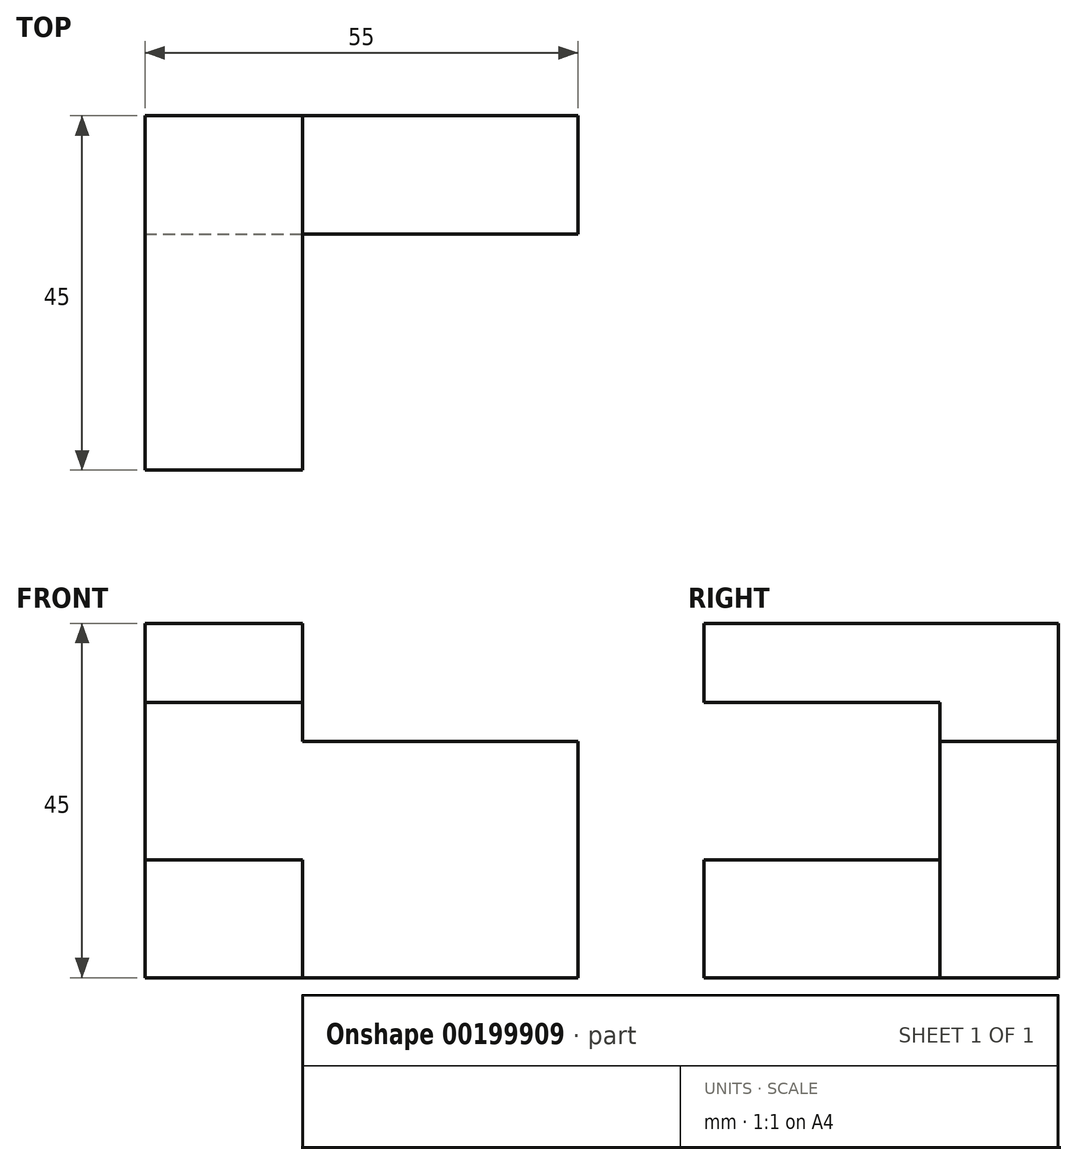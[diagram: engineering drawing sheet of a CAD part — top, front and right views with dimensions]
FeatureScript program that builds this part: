
annotation { "Feature Type Name" : "Feature", "Feature Type Description" : "" }
export const myFeature = defineFeature(function(context is Context, id is Id, definition is map)
    precondition{}
    {
        {
            var Q0;
            Q0=qCreatedBy(makeId("Front.planeOp"),FACE);
            var sketch = newSketch(context, id + "F0", { "sketchPlane" : qUnion([Q0])});
            skLineSegment(sketch, "E0", {"start": v(0, 0) * mm, "end": v(0, 45) * mm});
            skLineSegment(sketch, "E1", {"start": v(0, 45) * mm, "end": v(20, 45) * mm});
            skLineSegment(sketch, "E2", {"start": v(55, 30) * mm, "end": v(55, 0) * mm});
            skLineSegment(sketch, "E3", {"start": v(55, 0) * mm, "end": v(0, 0) * mm});
            skLineSegment(sketch, "E4", {"start": v(0, 15) * mm, "end": v(0, 0) * mm});
            skLineSegment(sketch, "E5", {"start": v(0, 15) * mm, "end": v(20, 15) * mm});
            skLineSegment(sketch, "E6", {"start": v(20, 15) * mm, "end": v(20, 0) * mm});
            skLineSegment(sketch, "E7", {"start": v(0, 15) * mm, "end": v(0, 35) * mm});
            skLineSegment(sketch, "E8", {"start": v(0, 35) * mm, "end": v(20, 35) * mm});
            skLineSegment(sketch, "E9", {"start": v(20, 35) * mm, "end": v(20, 45) * mm});
            skLineSegment(sketch, "E10", {"start": v(55, 30) * mm, "end": v(20, 30) * mm});
            skLineSegment(sketch, "E11", {"start": v(20, 30) * mm, "end": v(20, 35) * mm});
            skSolve(sketch);
        }
        {
            var Q0;
            {var subQ0=sQuery(id+"F0.wireOp",EDGE,"E4");Q0=makeQuery(id+"F0.imprint","IMPRINT",FACE,{"disambiguationData":[TD([[makeQuery(id+"F0.imprint","IMPRINT",EDGE,{"derivedFrom":subQ0}),1.0]])]});}
            var Q1;
            {var subQ2=sQuery(id+"F0.wireOp",EDGE,"E2");Q1=makeQuery(id+"F0.imprint","IMPRINT",FACE,{"disambiguationData":[TD([[makeQuery(id+"F0.imprint","IMPRINT",EDGE,{"derivedFrom":subQ2}),-1.0]])]});}
            var Q2;
            Q2=makeQuery(id+"F0.imprint","IMPRINT",FACE,{"disambiguationData":[TD([[makeQuery(id+"F0.imprint","IMPRINT",EDGE,{"derivedFrom":sQuery(id+"F0.wireOp",EDGE,"E0")}),-1.0]])]});
            extrude(context, id + "F1", {"entities" : qUnion([Q0, Q1, Q2]), "oppositeDirection" : true, "depth" : 45 * mm});
        }
        {
            var Q0;
            {var subQ2=sQuery(id+"F0.wireOp",EDGE,"E2");Q0=makeQuery(id+"F0.imprint","IMPRINT",FACE,{"disambiguationData":[TD([[makeQuery(id+"F0.imprint","IMPRINT",EDGE,{"derivedFrom":subQ2}),-1.0]])]});}
            extrude(context, id + "F2", {"entities" : qUnion([Q0]), "operationType" : NewBodyOperationType.REMOVE, "oppositeDirection" : true, "depth" : 30 * mm});
        }
    });
